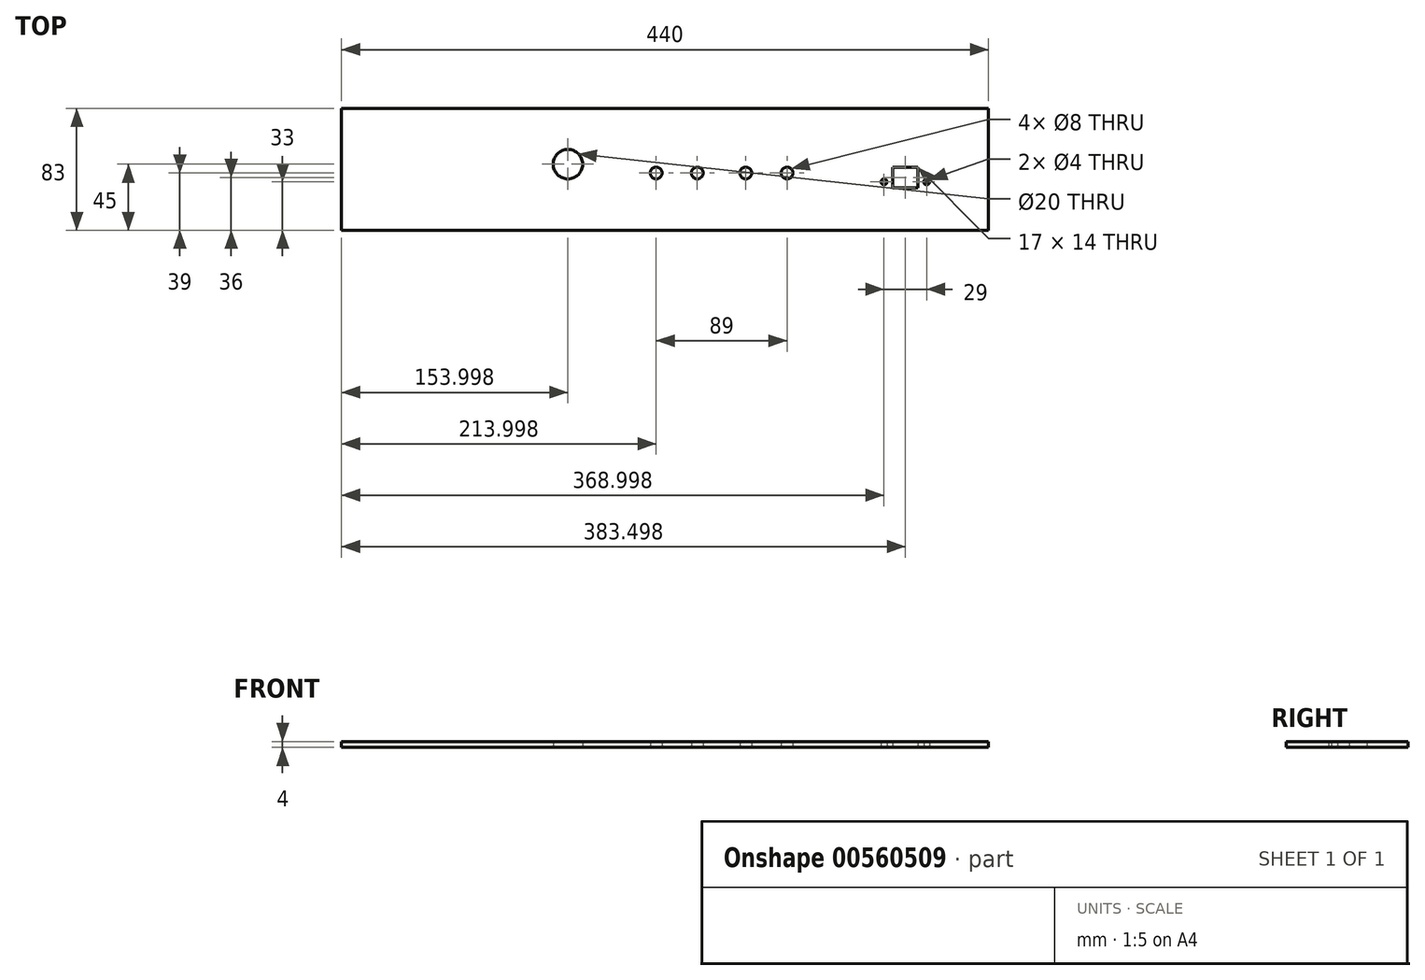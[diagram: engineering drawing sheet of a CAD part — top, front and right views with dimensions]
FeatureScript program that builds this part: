
annotation { "Feature Type Name" : "Feature", "Feature Type Description" : "" }
export const myFeature = defineFeature(function(context is Context, id is Id, definition is map)
    precondition{}
    {
        {
            var Q0;
            Q0=qCreatedBy(makeId("Top.planeOp"),FACE);
            var sketch = newSketch(context, id + "F0", { "sketchPlane" : qUnion([Q0])});
            skLineSegment(sketch, "E0.bottom", {"start": v(-226.44, 38) * mm, "end": v(213.56, 38) * mm});
            skLineSegment(sketch, "E0.top", {"start": v(-226.44, -45) * mm, "end": v(213.56, -45) * mm});
            skLineSegment(sketch, "E0.left", {"start": v(-226.44, 38) * mm, "end": v(-226.44, -45) * mm});
            skLineSegment(sketch, "E0.right", {"start": v(213.56, 38) * mm, "end": v(213.56, -45) * mm});
            skLineSegment(sketch, "E1.bottom", {"start": v(148.56, -2) * mm, "end": v(165.56, -2) * mm});
            skLineSegment(sketch, "E1.top", {"start": v(148.56, -16) * mm, "end": v(165.56, -16) * mm});
            skLineSegment(sketch, "E1.left", {"start": v(148.56, -2) * mm, "end": v(148.56, -16) * mm});
            skLineSegment(sketch, "E1.right", {"start": v(165.56, -2) * mm, "end": v(165.56, -16) * mm});
            skPoint(sketch, "E2.firstSnap0", {"position": v(157.06, -2) * mm});
            skCircle(sketch, "E3", {"center": v(171.56, -12) * mm, "radius": 2 * mm});
            skCircle(sketch, "E4.MirrorC", {"center": v(142.56, -12) * mm, "radius": 2 * mm});
            skCircle(sketch, "E5.MirrorC", {"center": v(15.56, -6) * mm, "radius": 4 * mm});
            skCircle(sketch, "E6.MirrorC", {"center": v(48.56, -6) * mm, "radius": 4 * mm});
            skCircle(sketch, "E7.MirrorC", {"center": v(-12.44, -6) * mm, "radius": 4 * mm});
            skCircle(sketch, "E8.MirrorC", {"center": v(76.56, -6) * mm, "radius": 4 * mm});
            skCircle(sketch, "E9", {"center": v(-72.44, 0) * mm, "radius": 10 * mm});
            skSolve(sketch);
        }
        {
            var Q0;
            Q0=makeQuery(id+"F0.imprint","IMPRINT",FACE,{"disambiguationData":[TD([[makeQuery(id+"F0.imprint","IMPRINT",EDGE,{"derivedFrom":sQuery(id+"F0.wireOp",EDGE,"E0.bottom")}),-1.0]])]});
            extrude(context, id + "F1", {"entities" : qUnion([Q0]), "depth" : 4 * mm, "offsetDistance" : 25 * mm});
        }
    });
